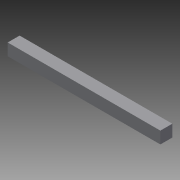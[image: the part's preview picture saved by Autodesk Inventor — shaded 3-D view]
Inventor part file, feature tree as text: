
AUTODESK INVENTOR PART (.ipt)
format: ipt  version: 2015 (Build 190159000, 159)  size: 67,584 bytes
history: native  units: in
note: dims shown in document units (in); Inventor stores cm internally (conversion verified against a paired STEP export)
features: extrude x1, sketch x1
ambient origin geometry x8: Origin, YZ Plane, XZ Plane, XY Plane, X Axis, Y Axis, Z Axis, Center Point
bodies: Solid1 (feature_tree)
feature tree (2):
  extrude  "Extrusion1"  Depth=0.75in
  sketch  "Sketch1"  dims[d0=0.75in d1=0.75in d2=9.575in d3=0.0in]
